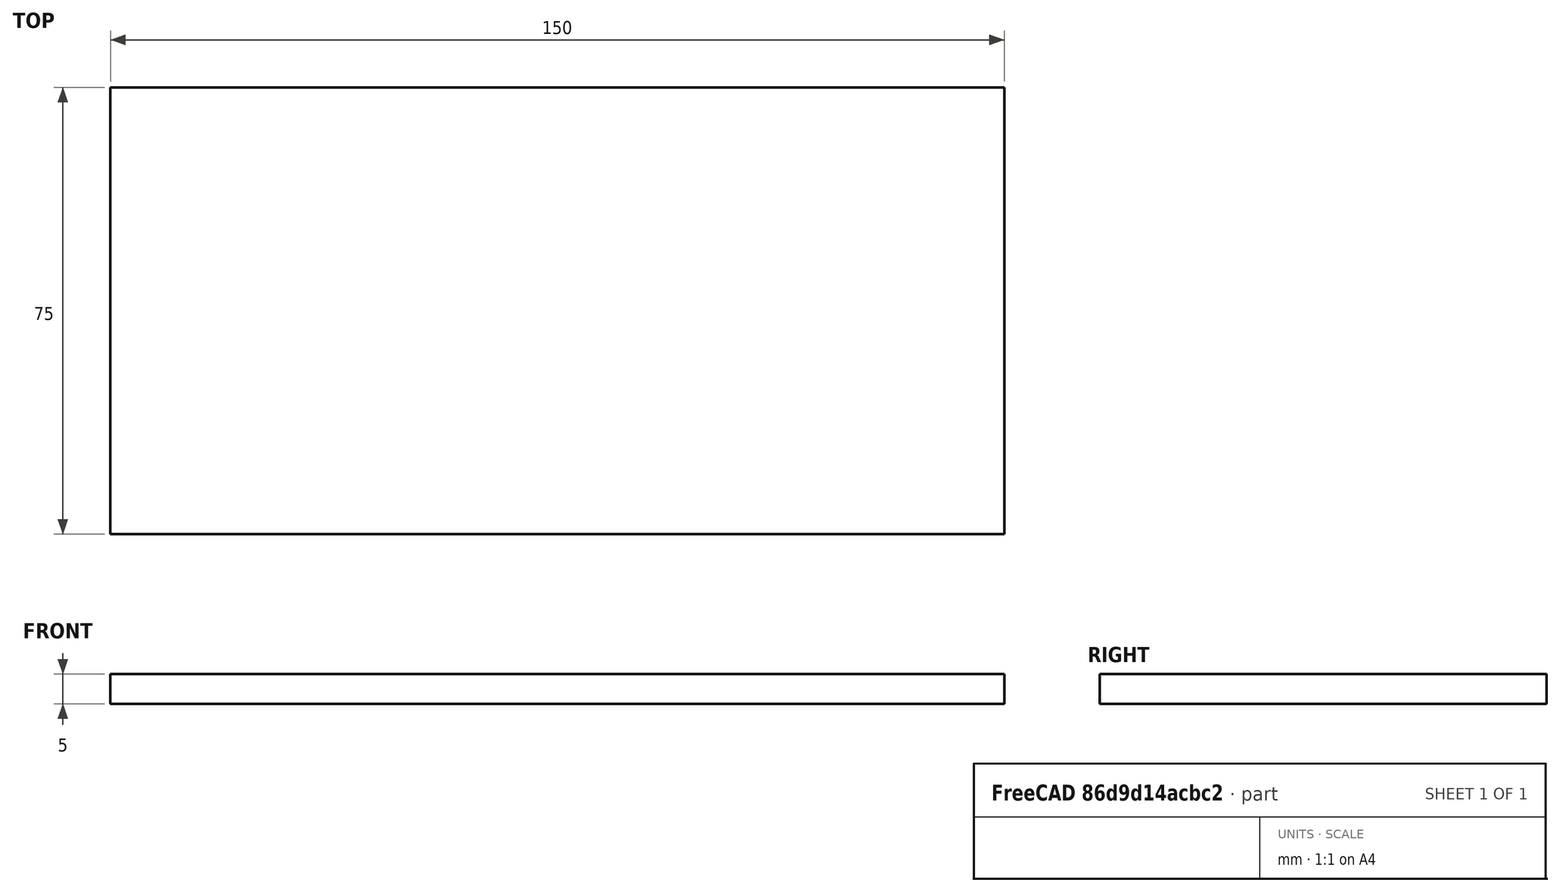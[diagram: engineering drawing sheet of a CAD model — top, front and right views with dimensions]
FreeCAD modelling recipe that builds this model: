
FCSTD DOCUMENT  (FreeCAD 0.19R24291 (Git))
Label: Base_robot
License: All rights reserved
LicenseURL: http://en.wikipedia.org/wiki/All_rights_reserved
objects: Sketcher::SketchObject×1, PartDesign::Pad×1, PartDesign::Body×1
note: 4 computed .brp shape members not serialized (recipe doc carries the construction recipe); baked Part::Feature solids carry a one-line shape summary decoded from their .brp

FEATURE [Sketcher::SketchObject] Sketch
  FullyConstrained = false
  MapMode = 5
  Support = -> [XY_Plane]
  sketch-geometry (4):
    g0: LineSegment StartX=-36.1738 StartY=-17.1935 StartZ=0 EndX=-36.1738 EndY=57.8065 EndZ=0
    g1: LineSegment StartX=-36.1738 StartY=57.8065 StartZ=0 EndX=113.826 EndY=57.8065 EndZ=0
    g2: LineSegment StartX=113.826 StartY=57.8065 StartZ=0 EndX=113.826 EndY=-17.1935 EndZ=0
    g3: LineSegment StartX=113.826 StartY=-17.1935 StartZ=0 EndX=-36.1738 EndY=-17.1935 EndZ=0
  constraints (10):
    c: Vertical(g0)
    c: DistanceY(g0,g0) = 75
    c: Coincident(g1,g0)
    c: Horizontal(g1)
    c: DistanceX(g1,g1) = 150
    c: Coincident(g2,g1)
    c: Vertical(g2)
    c: Equal(g0,g2)
    c: Coincident(g3,g2)
    c: Coincident(g3,g0)
FEATURE [PartDesign::Pad] Pad
  Direction = (1,1,1)
  Length = 5
  Length2 = 100
  Profile = -> Sketch
  Type = 0
FEATURE [PartDesign::Body] Body  label="base_DieGo"
  Group = -> [Sketch,Pad]
  Origin = -> Origin
  Tip = -> Pad
